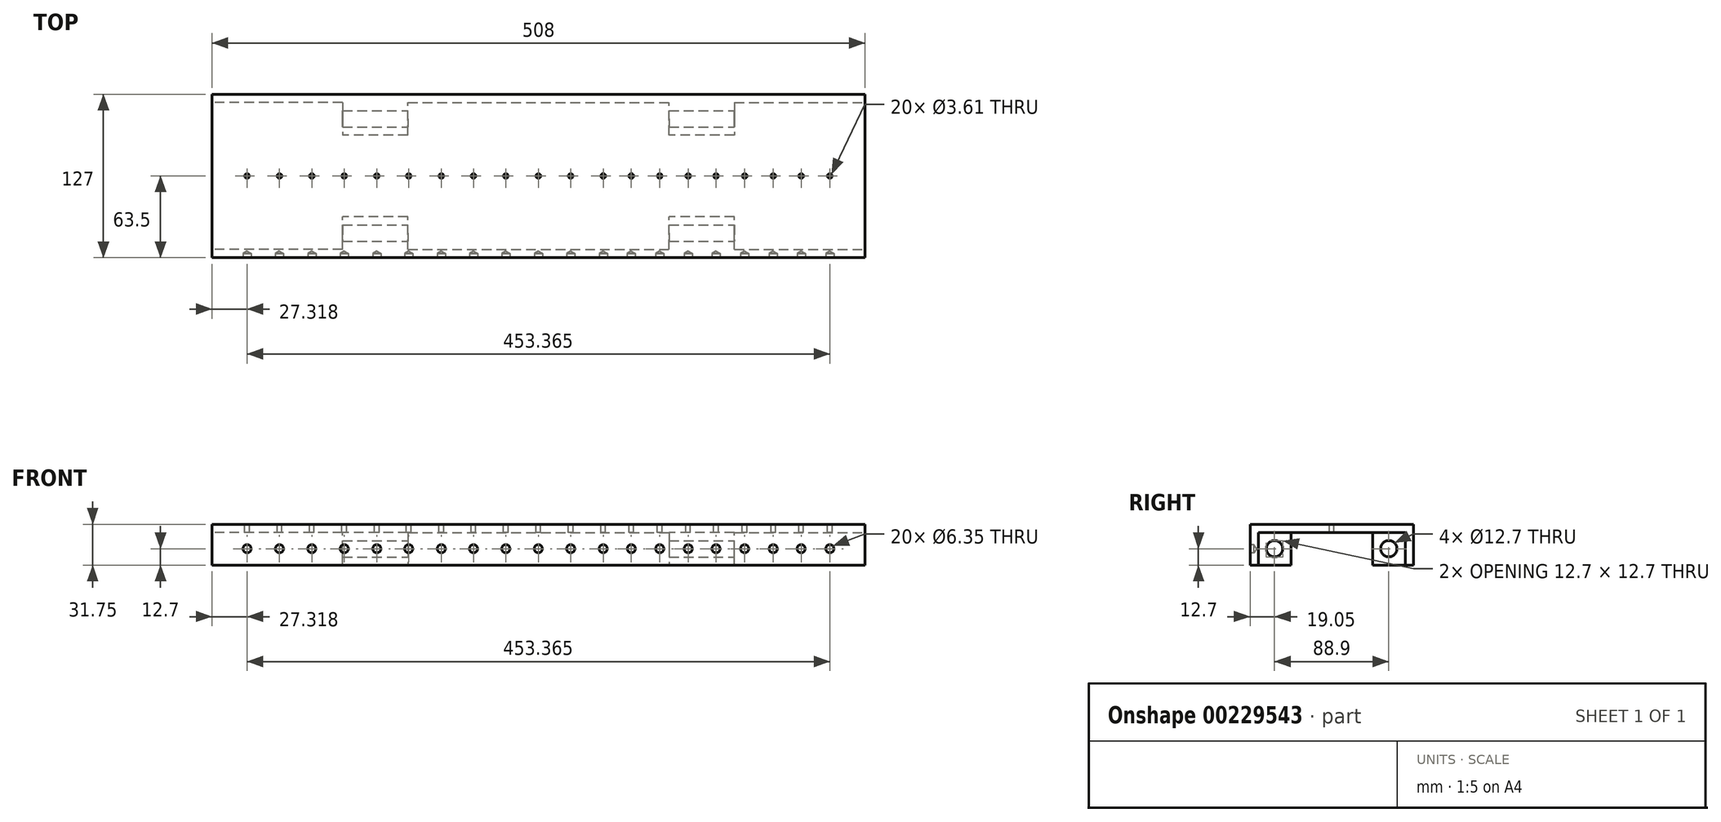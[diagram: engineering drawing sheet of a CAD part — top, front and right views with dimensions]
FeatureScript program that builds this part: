
annotation { "Feature Type Name" : "Feature", "Feature Type Description" : "" }
export const myFeature = defineFeature(function(context is Context, id is Id, definition is map)
    precondition{}
    {
        {
            var Q0;
            Q0=qCreatedBy(makeId("Right.planeOp"),FACE);
            var sketch = newSketch(context, id + "F0", { "sketchPlane" : qUnion([Q0])});
            skLineSegment(sketch, "E0", {"start": v(-57.15, 0) * mm, "end": v(57.15, 0) * mm});
            skLineSegment(sketch, "E1", {"start": v(57.15, 0) * mm, "end": v(57.15, -25.4) * mm});
            skLineSegment(sketch, "E2", {"start": v(57.15, -25.4) * mm, "end": v(63.5, -25.4) * mm});
            skLineSegment(sketch, "E3", {"start": v(63.5, -25.4) * mm, "end": v(63.5, 6.35) * mm});
            skLineSegment(sketch, "E4", {"start": v(63.5, 6.35) * mm, "end": v(-63.5, 6.35) * mm});
            skLineSegment(sketch, "E5", {"start": v(-63.5, 6.35) * mm, "end": v(-63.5, -25.4) * mm});
            skLineSegment(sketch, "E6", {"start": v(-63.5, -25.4) * mm, "end": v(-57.15, -25.4) * mm});
            skLineSegment(sketch, "E7", {"start": v(-57.15, 0) * mm, "end": v(-57.15, -25.4) * mm});
            skLineSegment(sketch, "E8", {"start": v(-57.15, -25.4) * mm, "end": v(-31.75, -25.4) * mm});
            skLineSegment(sketch, "E9", {"start": v(-31.75, -25.4) * mm, "end": v(-31.75, 0) * mm});
            skLineSegment(sketch, "E10", {"start": v(57.15, -25.4) * mm, "end": v(31.75, -25.4) * mm});
            skLineSegment(sketch, "E11", {"start": v(31.75, -25.4) * mm, "end": v(31.75, 0) * mm});
            skSolve(sketch);
        }
        {
            var Q0;
            Q0 = qSketchRegion(id + "F0", true);
            extrude(context, id + "F1", {"entities" : qUnion([Q0]), "depth" : 254 * mm, "hasSecondDirection" : true, "secondDirectionOppositeDirection" : true, "secondDirectionDepth" : 254 * mm});
        }
        {
            var Q0;
            Q0=makeQuery(id+"F1.opExtrude","SWEPT_FACE",FACE,{"disambiguationData":[OSD([sQuery(id+"F0.wireOp",EDGE,"E4")])]});
            var sketch = newSketch(context, id + "F2", { "sketchPlane" : qUnion([Q0])});
            skPoint(sketch, "E12", {"position": v(226.68, 0) * mm});
            skPoint(sketch, "E13", {"position": v(204.4, 0) * mm});
            skPoint(sketch, "E14", {"position": v(182.66, 0) * mm});
            skPoint(sketch, "E15", {"position": v(160.41, 0) * mm});
            skPoint(sketch, "E16", {"position": v(138.14, 0) * mm});
            skPoint(sketch, "E17", {"position": v(116.5, 0) * mm});
            skPoint(sketch, "E18", {"position": v(94.35, 0) * mm});
            skPoint(sketch, "E19", {"position": v(72.22, 0) * mm});
            skPoint(sketch, "E20", {"position": v(50.38, 0) * mm});
            skPoint(sketch, "E21", {"position": v(25.08, 0) * mm});
            skPoint(sketch, "E22", {"position": v(-0.06, 0) * mm});
            skPoint(sketch, "E23", {"position": v(-25.39, 0) * mm});
            skPoint(sketch, "E24", {"position": v(-50.53, 0) * mm});
            skPoint(sketch, "E25", {"position": v(-75.55, 0) * mm});
            skPoint(sketch, "E26", {"position": v(-100.95, 0) * mm});
            skPoint(sketch, "E27", {"position": v(-125.74, 0) * mm});
            skPoint(sketch, "E28", {"position": v(-151.1, 0) * mm});
            skPoint(sketch, "E29", {"position": v(-176.29, 0) * mm});
            skPoint(sketch, "E30", {"position": v(-201.49, 0) * mm});
            skPoint(sketch, "E31", {"position": v(-226.68, 0) * mm});
            skSolve(sketch);
        }
        {
            var Q0;
            Q0=sQuery(id+"F2.wireOp",VERTEX,"E31");
            var Q1;
            Q1=sQuery(id+"F2.wireOp",VERTEX,"E30");
            var Q2;
            Q2=sQuery(id+"F2.wireOp",VERTEX,"E29");
            var Q3;
            Q3=sQuery(id+"F2.wireOp",VERTEX,"E28");
            var Q4;
            Q4=sQuery(id+"F2.wireOp",VERTEX,"E27");
            var Q5;
            Q5=sQuery(id+"F2.wireOp",VERTEX,"E26");
            var Q6;
            Q6=sQuery(id+"F2.wireOp",VERTEX,"E25");
            var Q7;
            Q7=sQuery(id+"F2.wireOp",VERTEX,"E24");
            var Q8;
            Q8=sQuery(id+"F2.wireOp",VERTEX,"E23");
            var Q9;
            Q9=sQuery(id+"F2.wireOp",VERTEX,"E22");
            var Q10;
            Q10=sQuery(id+"F2.wireOp",VERTEX,"E21");
            var Q11;
            Q11=sQuery(id+"F2.wireOp",VERTEX,"E20");
            var Q12;
            Q12=sQuery(id+"F2.wireOp",VERTEX,"E19");
            var Q13;
            Q13=sQuery(id+"F2.wireOp",VERTEX,"E18");
            var Q14;
            Q14=sQuery(id+"F2.wireOp",VERTEX,"E17");
            var Q15;
            Q15=sQuery(id+"F2.wireOp",VERTEX,"E16");
            var Q16;
            Q16=sQuery(id+"F2.wireOp",VERTEX,"E15");
            var Q17;
            Q17=sQuery(id+"F2.wireOp",VERTEX,"E14");
            var Q18;
            Q18=sQuery(id+"F2.wireOp",VERTEX,"E13");
            var Q19;
            Q19=sQuery(id+"F2.wireOp",VERTEX,"E12");
            var Q20;
            Q20=makeQuery(id+"F1.opExtrude","SWEPT_BODY",BODY,{"disambiguationData":[OSD([sQuery(id+"F0.wireOp",EDGE,"E0"),sQuery(id+"F0.wireOp",EDGE,"E1"),sQuery(id+"F0.wireOp",EDGE,"E2"),sQuery(id+"F0.wireOp",EDGE,"E3"),sQuery(id+"F0.wireOp",EDGE,"E4"),sQuery(id+"F0.wireOp",EDGE,"E5"),sQuery(id+"F0.wireOp",EDGE,"E6"),sQuery(id+"F0.wireOp",EDGE,"E7")])]});
            hole(context, id + "F3", {"style" : HoleStyle.SIMPLE, "endStyle" : HoleEndStyle.THROUGH, "holeDiameter" : 3.6 * mm, "startFromSketch" : true, "locations" : qUnion([Q0, Q1, Q2, Q3, Q4, Q5, Q6, Q7, Q8, Q9, Q10, Q11, Q12, Q13, Q14, Q15, Q16, Q17, Q18, Q19]), "scope" : qUnion([Q20]), "isTappedThrough" : true});
        }
        {
            var Q0;
            Q0=makeQuery(id+"F1.opExtrude","SWEPT_FACE",FACE,{"disambiguationData":[OSD([sQuery(id+"F0.wireOp",EDGE,"E5")])]});
            var sketch = newSketch(context, id + "F4", { "sketchPlane" : qUnion([Q0])});
            skPoint(sketch, "E32", {"position": v(226.68, -12.7) * mm});
            skPoint(sketch, "E33", {"position": v(204.4, -12.7) * mm});
            skPoint(sketch, "E34", {"position": v(182.66, -12.7) * mm});
            skPoint(sketch, "E35", {"position": v(160.41, -12.7) * mm});
            skPoint(sketch, "E36", {"position": v(138.14, -12.7) * mm});
            skPoint(sketch, "E37", {"position": v(116.5, -12.7) * mm});
            skPoint(sketch, "E38", {"position": v(94.35, -12.7) * mm});
            skPoint(sketch, "E39", {"position": v(72.22, -12.7) * mm});
            skPoint(sketch, "E40", {"position": v(50.38, -12.7) * mm});
            skPoint(sketch, "E41", {"position": v(25.08, -12.7) * mm});
            skPoint(sketch, "E42", {"position": v(-0.06, -12.7) * mm});
            skPoint(sketch, "E43", {"position": v(-25.39, -12.7) * mm});
            skPoint(sketch, "E44", {"position": v(-50.53, -12.7) * mm});
            skPoint(sketch, "E45", {"position": v(-75.55, -12.7) * mm});
            skPoint(sketch, "E46", {"position": v(-100.95, -12.7) * mm});
            skPoint(sketch, "E47", {"position": v(-125.74, -12.7) * mm});
            skPoint(sketch, "E48", {"position": v(-151.1, -12.7) * mm});
            skPoint(sketch, "E49", {"position": v(-176.29, -12.7) * mm});
            skPoint(sketch, "E50", {"position": v(-201.49, -12.7) * mm});
            skPoint(sketch, "E51", {"position": v(-226.68, -12.7) * mm});
            skSolve(sketch);
        }
        {
            var Q0;
            Q0=makeQuery(id+"F1.opExtrude","CAP_FACE",FACE,{"disambiguationData":[OSD([sQuery(id+"F0.wireOp",EDGE,"E0"),sQuery(id+"F0.wireOp",EDGE,"E2"),sQuery(id+"F0.wireOp",EDGE,"E3"),sQuery(id+"F0.wireOp",EDGE,"E4"),sQuery(id+"F0.wireOp",EDGE,"E5"),sQuery(id+"F0.wireOp",EDGE,"E6"),sQuery(id+"F0.wireOp",EDGE,"E8"),sQuery(id+"F0.wireOp",EDGE,"E9"),sQuery(id+"F0.wireOp",EDGE,"E10"),sQuery(id+"F0.wireOp",EDGE,"E11")])],"isStart":false});
            var sketch = newSketch(context, id + "F5", { "sketchPlane" : qUnion([Q0])});
            skPoint(sketch, "E52", {"position": v(-44.45, -12.7) * mm});
            skPoint(sketch, "E53", {"position": v(44.45, -12.7) * mm});
            skSolve(sketch);
        }
        {
            var Q0;
            Q0=sQuery(id+"F5.wireOp",VERTEX,"E52");
            var Q1;
            Q1=sQuery(id+"F5.wireOp",VERTEX,"E53");
            var Q2;
            Q2=makeQuery(id+"F1.opExtrude","SWEPT_BODY",BODY,{"disambiguationData":[OSD([sQuery(id+"F0.wireOp",EDGE,"E0"),sQuery(id+"F0.wireOp",EDGE,"E2"),sQuery(id+"F0.wireOp",EDGE,"E3"),sQuery(id+"F0.wireOp",EDGE,"E4"),sQuery(id+"F0.wireOp",EDGE,"E5"),sQuery(id+"F0.wireOp",EDGE,"E6"),sQuery(id+"F0.wireOp",EDGE,"E8"),sQuery(id+"F0.wireOp",EDGE,"E9"),sQuery(id+"F0.wireOp",EDGE,"E10"),sQuery(id+"F0.wireOp",EDGE,"E11")])]});
            hole(context, id + "F6", {"style" : HoleStyle.SIMPLE, "endStyle" : HoleEndStyle.THROUGH, "holeDiameter" : 12.7 * mm, "startFromSketch" : true, "locations" : qUnion([Q0, Q1]), "scope" : qUnion([Q2]), "isTappedThrough" : true});
        }
        {
            var Q0;
            Q0=sQuery(id+"F4.wireOp",VERTEX,"E51");
            var Q1;
            Q1=sQuery(id+"F4.wireOp",VERTEX,"E50");
            var Q2;
            Q2=sQuery(id+"F4.wireOp",VERTEX,"E49");
            var Q3;
            Q3=sQuery(id+"F4.wireOp",VERTEX,"E48");
            var Q4;
            Q4=sQuery(id+"F4.wireOp",VERTEX,"E47");
            var Q5;
            Q5=sQuery(id+"F4.wireOp",VERTEX,"E46");
            var Q6;
            Q6=sQuery(id+"F4.wireOp",VERTEX,"E45");
            var Q7;
            Q7=sQuery(id+"F4.wireOp",VERTEX,"E44");
            var Q8;
            Q8=sQuery(id+"F4.wireOp",VERTEX,"E43");
            var Q9;
            Q9=sQuery(id+"F4.wireOp",VERTEX,"E42");
            var Q10;
            Q10=sQuery(id+"F4.wireOp",VERTEX,"E41");
            var Q11;
            Q11=sQuery(id+"F4.wireOp",VERTEX,"E40");
            var Q12;
            Q12=sQuery(id+"F4.wireOp",VERTEX,"E39");
            var Q13;
            Q13=sQuery(id+"F4.wireOp",VERTEX,"E38");
            var Q14;
            Q14=sQuery(id+"F4.wireOp",VERTEX,"E37");
            var Q15;
            Q15=sQuery(id+"F4.wireOp",VERTEX,"E36");
            var Q16;
            Q16=sQuery(id+"F4.wireOp",VERTEX,"E35");
            var Q17;
            Q17=sQuery(id+"F4.wireOp",VERTEX,"E34");
            var Q18;
            Q18=sQuery(id+"F4.wireOp",VERTEX,"E33");
            var Q19;
            Q19=sQuery(id+"F4.wireOp",VERTEX,"E32");
            var Q20;
            Q20=makeQuery(id+"F1.opExtrude","SWEPT_BODY",BODY,{"disambiguationData":[OSD([sQuery(id+"F0.wireOp",EDGE,"E0"),sQuery(id+"F0.wireOp",EDGE,"E2"),sQuery(id+"F0.wireOp",EDGE,"E3"),sQuery(id+"F0.wireOp",EDGE,"E4"),sQuery(id+"F0.wireOp",EDGE,"E5"),sQuery(id+"F0.wireOp",EDGE,"E6"),sQuery(id+"F0.wireOp",EDGE,"E8"),sQuery(id+"F0.wireOp",EDGE,"E9"),sQuery(id+"F0.wireOp",EDGE,"E10"),sQuery(id+"F0.wireOp",EDGE,"E11")])]});
            hole(context, id + "F7", {"style" : HoleStyle.SIMPLE, "endStyle" : HoleEndStyle.BLIND, "holeDiameter" : 6.35 * mm, "holeDepth" : 3.17 * mm, "startFromSketch" : true, "locations" : qUnion([Q0, Q1, Q2, Q3, Q4, Q5, Q6, Q7, Q8, Q9, Q10, Q11, Q12, Q13, Q14, Q15, Q16, Q17, Q18, Q19]), "scope" : qUnion([Q20])});
        }
        {
            var Q0;
            Q0=makeQuery(id+"F1.opExtrude","CAP_FACE",FACE,{"disambiguationData":[OSD([sQuery(id+"F0.wireOp",EDGE,"E0"),sQuery(id+"F0.wireOp",EDGE,"E2"),sQuery(id+"F0.wireOp",EDGE,"E3"),sQuery(id+"F0.wireOp",EDGE,"E4"),sQuery(id+"F0.wireOp",EDGE,"E5"),sQuery(id+"F0.wireOp",EDGE,"E6"),sQuery(id+"F0.wireOp",EDGE,"E8"),sQuery(id+"F0.wireOp",EDGE,"E9"),sQuery(id+"F0.wireOp",EDGE,"E10"),sQuery(id+"F0.wireOp",EDGE,"E11")])],"isStart":false});
            var sketch = newSketch(context, id + "F8", { "sketchPlane" : qUnion([Q0])});
            skLineSegment(sketch, "E54.bottom", {"start": v(-57.15, 0) * mm, "end": v(57.15, 0) * mm});
            skLineSegment(sketch, "E54.top", {"start": v(-57.15, -25.4) * mm, "end": v(57.15, -25.4) * mm});
            skLineSegment(sketch, "E54.left", {"start": v(-57.15, 0) * mm, "end": v(-57.15, -25.4) * mm});
            skLineSegment(sketch, "E54.right", {"start": v(57.15, 0) * mm, "end": v(57.15, -25.4) * mm});
            skSolve(sketch);
        }
        {
            var Q0;
            {var subQ1=sQuery(id+"F8.wireOp",EDGE,"E54.right");Q0=makeQuery(id+"F8.imprint","IMPRINT",FACE,{"disambiguationData":[TD([[makeQuery(id+"F8.imprint","IMPRINT",EDGE,{"derivedFrom":subQ1}),-1.0]])]});}
            var Q1;
            {var subQ0=sQuery(id+"F8.wireOp",EDGE,"E54.left");Q1=makeQuery(id+"F8.imprint","IMPRINT",FACE,{"disambiguationData":[TD([[makeQuery(id+"F8.imprint","IMPRINT",EDGE,{"derivedFrom":subQ0}),1.0]])]});}
            extrude(context, id + "F9", {"entities" : qUnion([Q0, Q1]), "operationType" : NewBodyOperationType.REMOVE, "oppositeDirection" : true, "depth" : 101.6 * mm});
        }
        {
            var Q0;
            Q0=makeQuery(id+"F1.opExtrude","CAP_FACE",FACE,{"disambiguationData":[OSD([sQuery(id+"F0.wireOp",EDGE,"E0"),sQuery(id+"F0.wireOp",EDGE,"E2"),sQuery(id+"F0.wireOp",EDGE,"E3"),sQuery(id+"F0.wireOp",EDGE,"E4"),sQuery(id+"F0.wireOp",EDGE,"E5"),sQuery(id+"F0.wireOp",EDGE,"E6"),sQuery(id+"F0.wireOp",EDGE,"E8"),sQuery(id+"F0.wireOp",EDGE,"E9"),sQuery(id+"F0.wireOp",EDGE,"E10"),sQuery(id+"F0.wireOp",EDGE,"E11")])],"isStart":true});
            var sketch = newSketch(context, id + "F10", { "sketchPlane" : qUnion([Q0])});
            skLineSegment(sketch, "E55.bottom", {"start": v(-57.15, 0) * mm, "end": v(57.15, 0) * mm});
            skLineSegment(sketch, "E55.top", {"start": v(-57.15, -25.4) * mm, "end": v(57.15, -25.4) * mm});
            skLineSegment(sketch, "E55.left", {"start": v(-57.15, 0) * mm, "end": v(-57.15, -25.4) * mm});
            skLineSegment(sketch, "E55.right", {"start": v(57.15, 0) * mm, "end": v(57.15, -25.4) * mm});
            skSolve(sketch);
        }
        {
            var Q0;
            {var subQ2=sQuery(id+"F10.wireOp",EDGE,"E55.left");Q0=makeQuery(id+"F10.imprint","IMPRINT",FACE,{"disambiguationData":[TD([[makeQuery(id+"F10.imprint","IMPRINT",EDGE,{"derivedFrom":subQ2}),1.0]])]});}
            var Q1;
            {var subQ0=sQuery(id+"F10.wireOp",EDGE,"E55.right");Q1=makeQuery(id+"F10.imprint","IMPRINT",FACE,{"disambiguationData":[TD([[makeQuery(id+"F10.imprint","IMPRINT",EDGE,{"derivedFrom":subQ0}),-1.0]])]});}
            extrude(context, id + "F11", {"entities" : qUnion([Q0, Q1]), "operationType" : NewBodyOperationType.REMOVE, "oppositeDirection" : true, "depth" : 101.6 * mm});
        }
        {
            var Q0;
            Q0=makeQuery(id+"F1.opExtrude","SWEPT_FACE",FACE,{"disambiguationData":[OSD([sQuery(id+"F0.wireOp",EDGE,"E6"),sQuery(id+"F0.wireOp",EDGE,"E8")])]});
            var sketch = newSketch(context, id + "F12", { "sketchPlane" : qUnion([Q0])});
            skLineSegment(sketch, "E56.bottom", {"start": v(-101.6, 57.15) * mm, "end": v(101.6, 57.15) * mm});
            skLineSegment(sketch, "E56.top", {"start": v(-101.6, -57.15) * mm, "end": v(101.6, -57.15) * mm});
            skLineSegment(sketch, "E56.left", {"start": v(-101.6, 57.15) * mm, "end": v(-101.6, -57.15) * mm});
            skLineSegment(sketch, "E56.right", {"start": v(101.6, 57.15) * mm, "end": v(101.6, -57.15) * mm});
            skLineSegment(sketch, "E57.0", {"start": v(152.4, -31.75) * mm, "end": v(-152.4, -31.75) * mm, "construction": true});
            skLineSegment(sketch, "E58", {"start": v(-101.6, -31.75) * mm, "end": v(101.6, -31.75) * mm});
            skSolve(sketch);
        }
        {
            var Q0;
            {var subQ0=sQuery(id+"F12.wireOp",EDGE,"E56.top");Q0=makeQuery(id+"F12.imprint","IMPRINT",FACE,{"disambiguationData":[TD([[makeQuery(id+"F12.imprint","IMPRINT",EDGE,{"derivedFrom":subQ0}),1.0]])]});}
            var Q1;
            {var subQ0=sQuery(id+"F12.wireOp",EDGE,"E56.bottom");Q1=makeQuery(id+"F12.imprint","IMPRINT",FACE,{"disambiguationData":[TD([[makeQuery(id+"F12.imprint","IMPRINT",EDGE,{"derivedFrom":subQ0}),-1.0]])]});}
            extrude(context, id + "F13", {"entities" : qUnion([Q0, Q1]), "operationType" : NewBodyOperationType.REMOVE, "oppositeDirection" : true, "depth" : 25.4 * mm});
        }
    });
